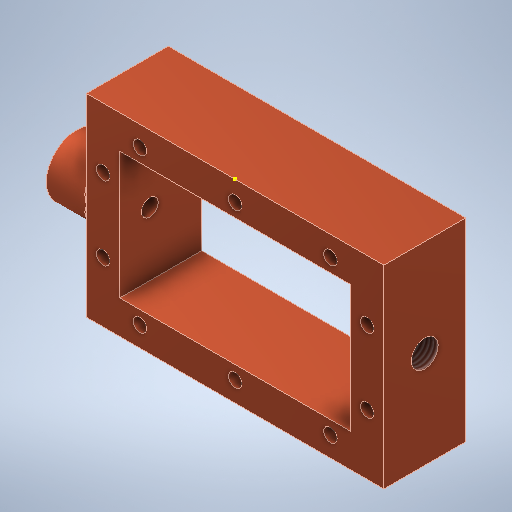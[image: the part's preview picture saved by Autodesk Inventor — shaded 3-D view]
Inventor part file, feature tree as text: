
AUTODESK INVENTOR PART (.ipt)
format: ipt  version: 2025.1 (Build 291241000, 241)  size: 335,360 bytes
history: native  units: mm
features: sketch x8, extrude x4, hole x3, plane x2, mirror x2, fillet x1, thread x1
ambient origin geometry x8: Origin, YZ Plane, XZ Plane, XY Plane, X Axis, Y Axis, Z Axis, Center Point
bodies: Volumenkörper1 (feature_tree)
feature tree (21):
  extrude  "Extrusion1"  Depth=58.0mm
  extrude  "Extrusion2"  Depth=24.5mm
  extrude  "Extrusion3"  Depth=24.5mm TaperAngle=0.0deg
  hole  "Bohrung1"  [1 undecoded]
  fillet  "Rundung1"  Radius=1.0mm
  sketch  "Skizze5"  dims[d11=5.0mm d12=6.0mm d13=10.0mm d14=17.0mm d15=90.0deg d16=8.0mm d17=0.0mm d18=1.0mm]
  extrude  "Extrusion4"  Depth=8.0mm
  plane  "Arbeitsebene1"
  thread  "Gewinde3"  [1 undecoded]
  hole  "Bohrung2"  [1 undecoded]
  mirror  "Spiegeln3"
  sketch  "Skizze10"  dims[d41=4.0mm d42=6.0mm d43=10.0mm d44=17.0mm d45=90.0deg d46=8.0mm d47=0.0mm d59=0.0mm d60=5.0mm d63=16.0mm d64=16.0mm d65=4.0mm d66=6.0mm d67=4.0mm d68=2.0mm d69=90.0deg d70=8.0mm d71=20.594885mm d72=11.0mm d73=11.0mm]
  plane  "Arbeitsebene3"
  hole  "Hole4"  [1 undecoded]
  mirror  "Mirror5"
  sketch  "Skizze1"  dims[d0=89.0mm d1=58.0mm]
  sketch  "Skizze2"  dims[d2=24.5mm d3=0.0mm d4=38.0mm]
  sketch  "Skizze3"  dims[d5=10.0mm d6=24.5mm d7=0.0mm]
  sketch  "Skizze4"  dims[d8=18.0mm d9=12.0mm d10=0.0mm]
  sketch  "Skizze6"  dims[d19=9.0mm d20=8.0mm d21=12.0mm d22=0.0mm]
  sketch  "Skizze9"  dims[d27=0.0mm d32=18.0mm d33=0.0mm]
note: 4 required parameter values undecoded (feature->parameter linkage not recoverable at this tier; creation-order binding heuristic only, values carry confidence <= 0.55)
